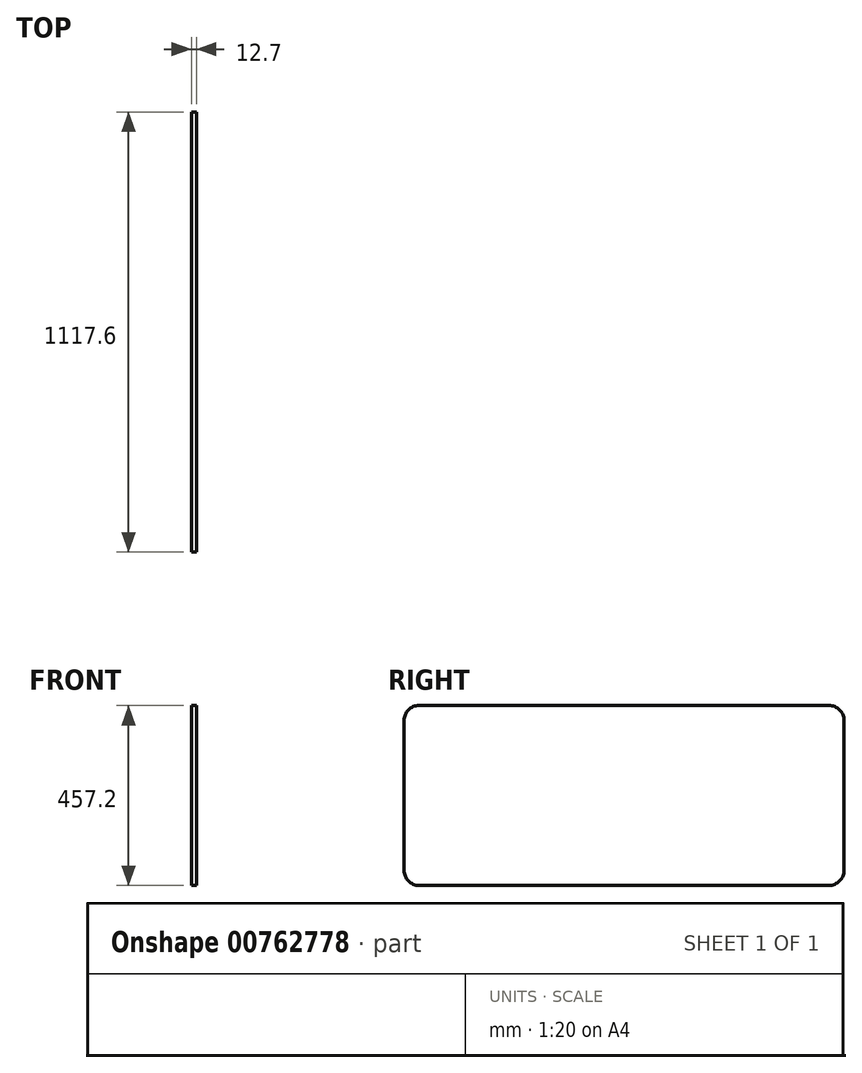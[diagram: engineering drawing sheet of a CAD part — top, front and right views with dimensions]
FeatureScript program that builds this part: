
annotation { "Feature Type Name" : "Feature", "Feature Type Description" : "" }
export const myFeature = defineFeature(function(context is Context, id is Id, definition is map)
    precondition{}
    {
        {
            var Q0;
            Q0=qCreatedBy(makeId("Right.planeOp"),FACE);
            var sketch = newSketch(context, id + "F0", { "sketchPlane" : qUnion([Q0])});
            skLineSegment(sketch, "E0.bottom", {"start": v(-1117.6, 448.35) * mm, "end": v(0, 448.35) * mm});
            skLineSegment(sketch, "E0.top", {"start": v(-1117.6, -8.85) * mm, "end": v(0, -8.85) * mm});
            skLineSegment(sketch, "E0.left", {"start": v(-1117.6, 448.35) * mm, "end": v(-1117.6, -8.85) * mm});
            skLineSegment(sketch, "E0.right", {"start": v(0, 448.35) * mm, "end": v(0, -8.85) * mm});
            skSolve(sketch);
        }
        {
            var Q0;
            Q0=makeQuery(id+"F0.imprint","IMPRINT",FACE,{"disambiguationData":[TD([[makeQuery(id+"F0.imprint","IMPRINT",EDGE,{"derivedFrom":sQuery(id+"F0.wireOp",EDGE,"E0.bottom")}),-1.0]])]});
            extrude(context, id + "F1", {"entities" : qUnion([Q0]), "depth" : 12.7 * mm, "offsetDistance" : 25.4 * mm});
        }
        {
            var Q0;
            Q0=makeQuery(id+"F1.opExtrude","SWEPT_EDGE",EDGE,{"disambiguationData":[OSD([sQuery(id+"F0.wireOp",EDGE,"E0.bottom"),sQuery(id+"F0.wireOp",EDGE,"E0.left")])]});
            var Q1;
            Q1=makeQuery(id+"F1.opExtrude","SWEPT_EDGE",EDGE,{"disambiguationData":[OSD([sQuery(id+"F0.wireOp",EDGE,"E0.bottom"),sQuery(id+"F0.wireOp",EDGE,"E0.right")])]});
            var Q2;
            Q2=makeQuery(id+"F1.opExtrude","SWEPT_EDGE",EDGE,{"disambiguationData":[OSD([sQuery(id+"F0.wireOp",EDGE,"E0.top"),sQuery(id+"F0.wireOp",EDGE,"E0.right")])]});
            var Q3;
            Q3=makeQuery(id+"F1.opExtrude","SWEPT_EDGE",EDGE,{"disambiguationData":[OSD([sQuery(id+"F0.wireOp",EDGE,"E0.top"),sQuery(id+"F0.wireOp",EDGE,"E0.left")])]});
            fillet(context, id + "F2", {"entities" : qUnion([Q0, Q1, Q2, Q3]), "radius" : 38.1 * mm, "tangentPropagation" : true, "allowEdgeOverflow" : false});
        }
    });
